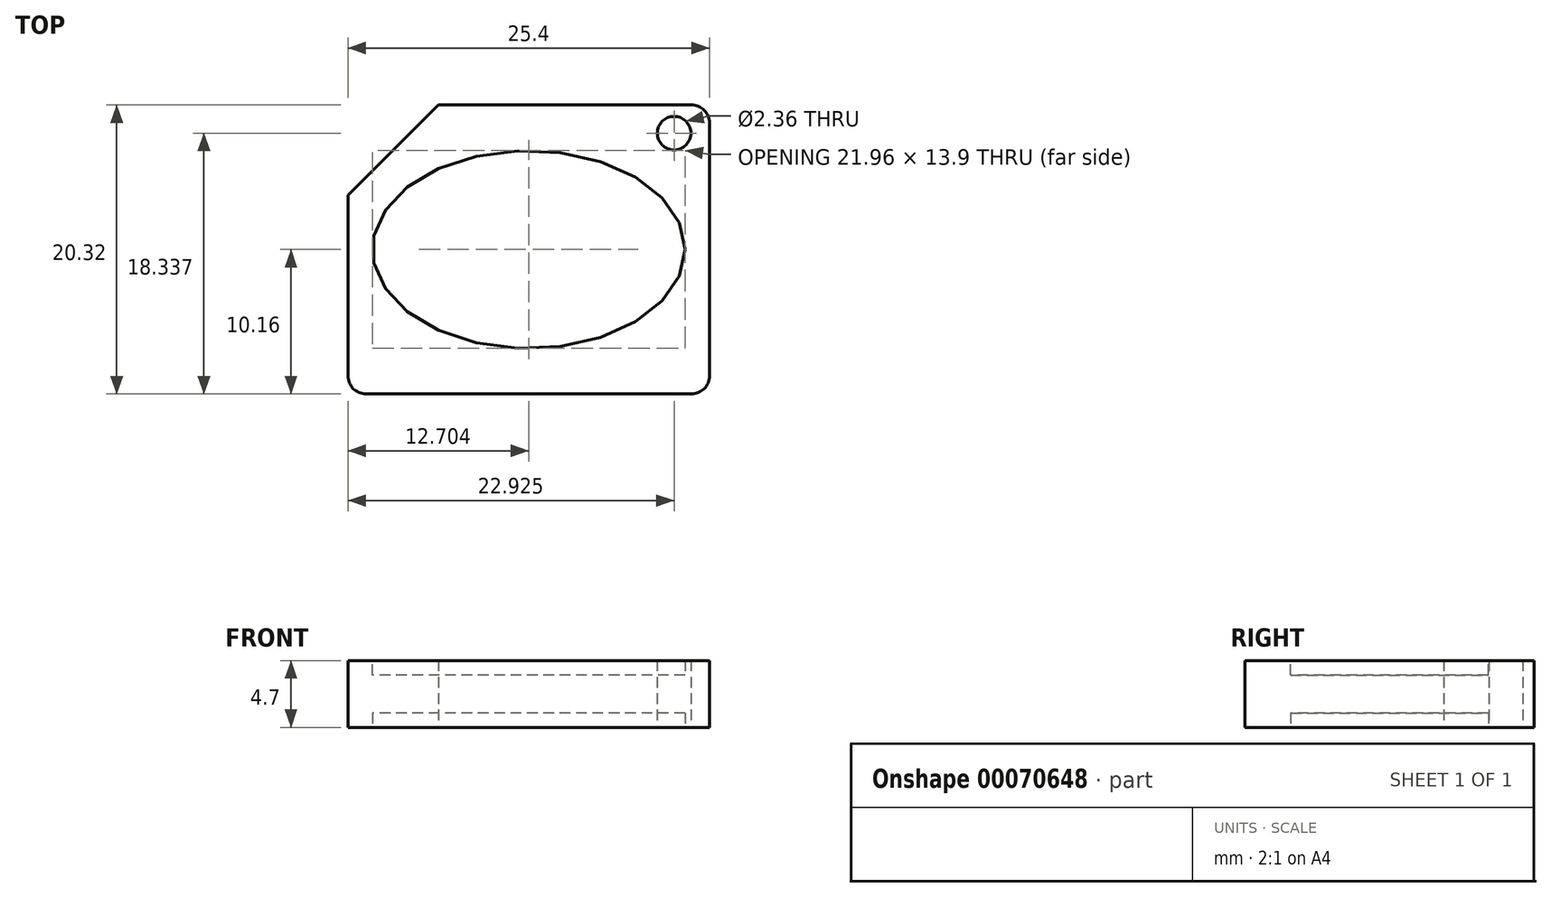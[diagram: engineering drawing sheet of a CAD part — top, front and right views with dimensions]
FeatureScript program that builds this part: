
annotation { "Feature Type Name" : "Feature", "Feature Type Description" : "" }
export const myFeature = defineFeature(function(context is Context, id is Id, definition is map)
    precondition{}
    {
        {
            var Q0;
            Q0=qCreatedBy(makeId("Top.planeOp"),FACE);
            var sketch = newSketch(context, id + "F0", { "sketchPlane" : qUnion([Q0])});
            skLineSegment(sketch, "E0.bottom", {"start": v(-2.97, 6.35) * mm, "end": v(-2.97, 6.35) * mm});
            skLineSegment(sketch, "E0.top", {"start": v(-1.7, -13.97) * mm, "end": v(21.16, -13.97) * mm});
            skLineSegment(sketch, "E0.right", {"start": v(22.43, 5.08) * mm, "end": v(22.43, -12.7) * mm});
            skLineSegment(sketch, "E1", {"start": v(3.38, 6.35) * mm, "end": v(-2.97, 0) * mm});
            skLineSegment(sketch, "E2", {"start": v(3.38, 6.35) * mm, "end": v(21.16, 6.35) * mm});
            skLineSegment(sketch, "E3", {"start": v(-2.97, 0) * mm, "end": v(-2.97, 0) * mm});
            skLineSegment(sketch, "E4", {"start": v(3.38, 6.35) * mm, "end": v(3.38, 6.35) * mm});
            skPoint(sketch, "E5.visualSharp", {"position": v(22.43, -13.97) * mm});
            skArc(sketch, "E5.filletArc", {"start": v(21.16, -13.97) * mm, "mid": v(22.06, -13.6) * mm, "end": v(22.43, -12.7) * mm});
            skPoint(sketch, "E6.visualSharp", {"position": v(22.43, 6.35) * mm});
            skArc(sketch, "E6.filletArc", {"start": v(22.43, 5.08) * mm, "mid": v(22.06, 5.98) * mm, "end": v(21.16, 6.35) * mm});
            skPoint(sketch, "E7.visualSharp", {"position": v(-2.97, -13.97) * mm});
            skArc(sketch, "E7.filletArc", {"start": v(-2.97, -12.7) * mm, "mid": v(-2.6, -13.6) * mm, "end": v(-1.7, -13.97) * mm});
            skEllipse(sketch, "E8", {"center": v(9.73, -3.8) * mm, "majorRadius": 10.98 * mm, "minorRadius": 6.95 * mm, "majorAxis": v(1, 0)});
            skLineSegment(sketch, "E9", {"start": v(-2.97, 0) * mm, "end": v(-2.97, -12.7) * mm});
            skCircle(sketch, "E10", {"center": v(19.95, 4.37) * mm, "radius": 1.18 * mm});
            skSolve(sketch);
        }
        {
            var Q0;
            Q0=makeQuery(id+"F0.imprint","IMPRINT",FACE,{"disambiguationData":[TD([[makeQuery(id+"F0.imprint","IMPRINT",EDGE,{"derivedFrom":sQuery(id+"F0.wireOp",EDGE,"E0.top")}),1.0]])]});
            extrude(context, id + "F1", {"entities" : qUnion([Q0]), "depth" : 4.7 * mm});
        }
        {
            var Q0;
            Q0=makeQuery(id+"F0.imprint","IMPRINT",FACE,{"disambiguationData":[TD([[makeQuery(id+"F0.imprint","IMPRINT",EDGE,{"derivedFrom":sQuery(id+"F0.wireOp",EDGE,"E8")}),1.0]])]});
            extrude(context, id + "F2", {"entities" : qUnion([Q0]), "operationType" : NewBodyOperationType.ADD, "depth" : 3.68 * mm});
        }
        {
            var Q0;
            Q0=makeQuery(id+"F0.imprint","IMPRINT",FACE,{"disambiguationData":[TD([[makeQuery(id+"F0.imprint","IMPRINT",EDGE,{"derivedFrom":sQuery(id+"F0.wireOp",EDGE,"E8")}),1.0]])]});
            extrude(context, id + "F4", {"entities" : qUnion([Q0]), "operationType" : NewBodyOperationType.REMOVE, "depth" : 1.02 * mm});
        }
    });
